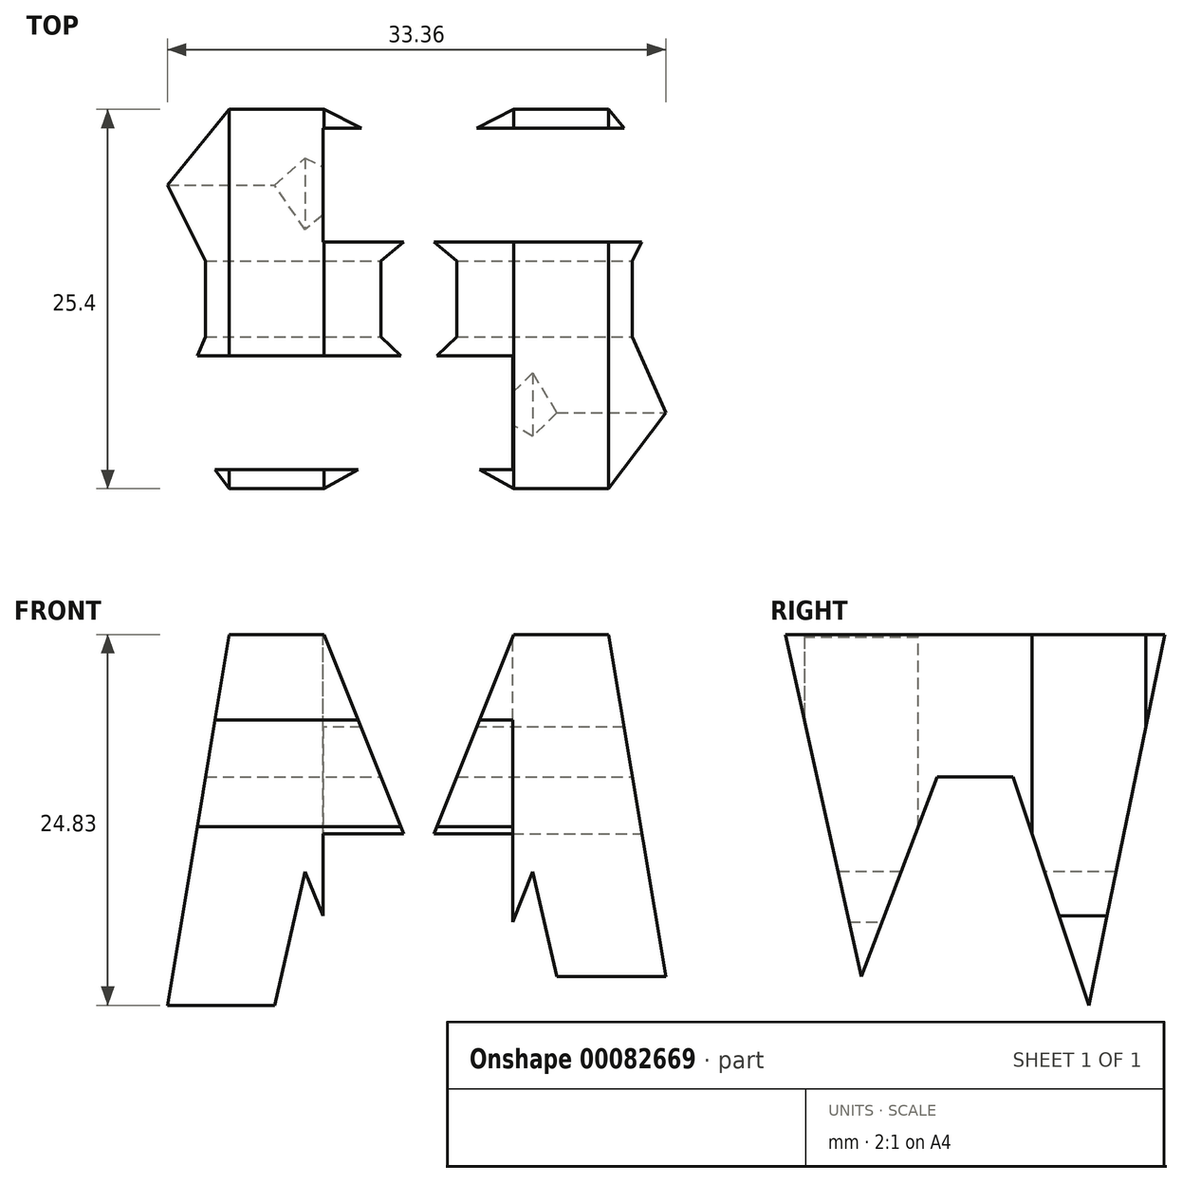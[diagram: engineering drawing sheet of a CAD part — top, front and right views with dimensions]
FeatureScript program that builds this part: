
annotation { "Feature Type Name" : "Feature", "Feature Type Description" : "" }
export const myFeature = defineFeature(function(context is Context, id is Id, definition is map)
    precondition{}
    {
        {
            var Q0;
            Q0=qCreatedBy(makeId("Front.planeOp"),FACE);
            var sketch = newSketch(context, id + "F0", { "sketchPlane" : qUnion([Q0])});
            skLineSegment(sketch, "E0.bottom", {"start": v(19.05, 19.05) * mm, "end": v(-19.05, 19.05) * mm});
            skLineSegment(sketch, "E0.top", {"start": v(19.05, -19.05) * mm, "end": v(-19.05, -19.05) * mm});
            skLineSegment(sketch, "E0.left", {"start": v(19.05, 19.05) * mm, "end": v(19.05, -19.05) * mm});
            skLineSegment(sketch, "E0.right", {"start": v(-19.05, 19.05) * mm, "end": v(-19.05, -19.05) * mm});
            skPoint(sketch, "E0.middle", {"position": v(0, 0) * mm});
            skSolve(sketch);
        }
        {
            var Q0;
            Q0 = qSketchRegion(id + "F0", true);
            extrude(context, id + "F1", {"entities" : qUnion([Q0]), "depth" : 38.1 * mm});
        }
        {
            var Q0;
            Q0=qCreatedBy(makeId("Front.planeOp"),FACE);
            cPlane(context, id + "F2", {"entities" : qUnion([Q0]), "cplaneType" : CPlaneType.OFFSET, "offset" : 38.1 * mm, "width" : 152.4 * mm, "height" : 152.4 * mm});
        }
        {
            var Q0;
            Q0=qCreatedBy(makeId("Top.planeOp"),FACE);
            cPlane(context, id + "F3", {"entities" : qUnion([Q0]), "cplaneType" : CPlaneType.OFFSET, "offset" : 38.1 * mm, "width" : 152.4 * mm, "height" : 152.4 * mm});
        }
        {
            var Q0;
            Q0=qCreatedBy(makeId("Right.planeOp"),FACE);
            cPlane(context, id + "F4", {"entities" : qUnion([Q0]), "cplaneType" : CPlaneType.OFFSET, "offset" : 38.1 * mm, "width" : 152.4 * mm, "height" : 152.4 * mm});
        }
        {
            var Q0;
            Q0=qCreatedBy(id+"F4.planeOp",FACE);
            var sketch = newSketch(context, id + "F5", { "sketchPlane" : qUnion([Q0])});
            skLineSegment(sketch, "E1", {"start": v(0, -19.05) * mm, "end": v(-38.1, -19.05) * mm});
            skLineSegment(sketch, "E2", {"start": v(-38.1, -19.05) * mm, "end": v(-38.1, 19.05) * mm});
            skLineSegment(sketch, "E3", {"start": v(-38.1, 19.05) * mm, "end": v(0, 19.05) * mm});
            skLineSegment(sketch, "E4", {"start": v(0, 19.05) * mm, "end": v(0, -19.05) * mm});
            skLineSegment(sketch, "E5", {"start": v(-38.1, 19.05) * mm, "end": v(-31.75, -19.05) * mm});
            skLineSegment(sketch, "E6", {"start": v(-31.75, -19.05) * mm, "end": v(-25.4, -19.05) * mm});
            skLineSegment(sketch, "E7", {"start": v(-25.4, -19.05) * mm, "end": v(-19.05, -3.17) * mm});
            skLineSegment(sketch, "E8", {"start": v(-19.05, -3.17) * mm, "end": v(-12.7, -19.05) * mm});
            skLineSegment(sketch, "E9", {"start": v(-12.7, -19.05) * mm, "end": v(-6.35, -19.05) * mm});
            skLineSegment(sketch, "E10", {"start": v(-6.35, -19.05) * mm, "end": v(0, 19.05) * mm});
            skLineSegment(sketch, "E11", {"start": v(0, 19.05) * mm, "end": v(-6.35, 19.05) * mm});
            skLineSegment(sketch, "E12", {"start": v(-6.35, 19.05) * mm, "end": v(-11.43, -5.78) * mm});
            skLineSegment(sketch, "E13", {"start": v(-11.43, -5.78) * mm, "end": v(-16.51, 9.53) * mm});
            skLineSegment(sketch, "E14", {"start": v(-16.5, 9.52) * mm, "end": v(-21.59, 9.52) * mm});
            skLineSegment(sketch, "E15", {"start": v(-21.59, 9.52) * mm, "end": v(-26.67, -3.85) * mm});
            skLineSegment(sketch, "E16", {"start": v(-26.67, -3.85) * mm, "end": v(-31.75, 19.05) * mm});
            skLineSegment(sketch, "E17", {"start": v(-31.75, 19.05) * mm, "end": v(-38.1, 19.05) * mm});
            skSolve(sketch);
        }
        {
            var Q0;
            Q0=qCreatedBy(id+"F2.planeOp",FACE);
            var sketch = newSketch(context, id + "F6", { "sketchPlane" : qUnion([Q0])});
            skLineSegment(sketch, "E18", {"start": v(-19.05, 19.05) * mm, "end": v(19.05, 19.05) * mm});
            skLineSegment(sketch, "E19", {"start": v(19.05, 19.05) * mm, "end": v(19.05, -19.05) * mm});
            skLineSegment(sketch, "E20", {"start": v(19.05, -19.05) * mm, "end": v(-19.05, -19.05) * mm});
            skLineSegment(sketch, "E21", {"start": v(-19.05, -19.05) * mm, "end": v(-19.05, 19.05) * mm});
            skLineSegment(sketch, "E22", {"start": v(-12.7, 19.05) * mm, "end": v(-19.05, -19.05) * mm});
            skLineSegment(sketch, "E23", {"start": v(-12.7, -19.05) * mm, "end": v(-7.62, 3.17) * mm});
            skLineSegment(sketch, "E24", {"start": v(-7.62, 3.17) * mm, "end": v(-2.54, -9.5) * mm});
            skLineSegment(sketch, "E25", {"start": v(-2.54, -9.5) * mm, "end": v(2.54, -9.5) * mm});
            skLineSegment(sketch, "E26", {"start": v(2.54, -9.5) * mm, "end": v(7.62, 3.17) * mm});
            skLineSegment(sketch, "E27", {"start": v(7.62, 3.18) * mm, "end": v(12.7, -19.05) * mm});
            skLineSegment(sketch, "E28", {"start": v(12.7, -19.05) * mm, "end": v(19.05, -19.05) * mm});
            skLineSegment(sketch, "E29", {"start": v(19.05, -19.05) * mm, "end": v(12.7, 19.05) * mm});
            skLineSegment(sketch, "E30", {"start": v(12.7, 19.05) * mm, "end": v(6.35, 19.05) * mm});
            skLineSegment(sketch, "E31", {"start": v(6.35, 19.05) * mm, "end": v(0, 3.17) * mm});
            skLineSegment(sketch, "E32", {"start": v(-6.35, 19.05) * mm, "end": v(-12.7, 19.05) * mm});
            skLineSegment(sketch, "E33", {"start": v(-6.35, 19.05) * mm, "end": v(0, 3.17) * mm});
            skSolve(sketch);
        }
        {
            var Q0;
            Q0=makeQuery(id+"F5.imprint","IMPRINT",FACE,{"disambiguationData":[TD([[makeQuery(id+"F5.imprint","IMPRINT",EDGE,{"derivedFrom":sQuery(id+"F5.wireOp",EDGE,"E3")}),-1.0]])]});
            var Q1;
            {var subQ0=sQuery(id+"F5.wireOp",EDGE,"E4");Q1=makeQuery(id+"F5.imprint","IMPRINT",FACE,{"disambiguationData":[TD([[makeQuery(id+"F5.imprint","IMPRINT",EDGE,{"derivedFrom":subQ0}),-1.0]])]});}
            var Q2;
            {var subQ0=sQuery(id+"F5.wireOp",EDGE,"E7");Q2=makeQuery(id+"F5.imprint","IMPRINT",FACE,{"disambiguationData":[TD([[makeQuery(id+"F5.imprint","IMPRINT",EDGE,{"derivedFrom":subQ0}),-1.0]])]});}
            var Q3;
            {var subQ0=sQuery(id+"F5.wireOp",EDGE,"E2");Q3=makeQuery(id+"F5.imprint","IMPRINT",FACE,{"disambiguationData":[TD([[makeQuery(id+"F5.imprint","IMPRINT",EDGE,{"derivedFrom":subQ0}),-1.0]])]});}
            extrude(context, id + "F7", {"entities" : qUnion([Q0, Q1, Q2, Q3]), "operationType" : NewBodyOperationType.REMOVE, "oppositeDirection" : true, "depth" : 58.42 * mm});
        }
        {
            var Q0;
            {var subQ0=sQuery(id+"F6.wireOp",EDGE,"E31");Q0=makeQuery(id+"F6.imprint","IMPRINT",FACE,{"disambiguationData":[TD([[makeQuery(id+"F6.imprint","IMPRINT",EDGE,{"derivedFrom":subQ0}),-1.0]])]});}
            var Q1;
            {var subQ0=sQuery(id+"F6.wireOp",EDGE,"E19");Q1=makeQuery(id+"F6.imprint","IMPRINT",FACE,{"disambiguationData":[TD([[makeQuery(id+"F6.imprint","IMPRINT",EDGE,{"derivedFrom":subQ0}),-1.0]])]});}
            var Q2;
            {var subQ1=sQuery(id+"F6.wireOp",EDGE,"E23");Q2=makeQuery(id+"F6.imprint","IMPRINT",FACE,{"disambiguationData":[TD([[makeQuery(id+"F6.imprint","IMPRINT",EDGE,{"derivedFrom":subQ1}),-1.0]])]});}
            var Q3;
            {var subQ0=sQuery(id+"F6.wireOp",EDGE,"E21");Q3=makeQuery(id+"F6.imprint","IMPRINT",FACE,{"disambiguationData":[TD([[makeQuery(id+"F6.imprint","IMPRINT",EDGE,{"derivedFrom":subQ0}),-1.0]])]});}
            extrude(context, id + "F8", {"entities" : qUnion([Q0, Q1, Q2, Q3]), "operationType" : NewBodyOperationType.REMOVE, "oppositeDirection" : true, "depth" : 38.1 * mm});
        }
        {
            var Q0;
            Q0=qCreatedBy(id+"F3.planeOp",FACE);
            var sketch = newSketch(context, id + "F9", { "sketchPlane" : qUnion([Q0])});
            skLineSegment(sketch, "E34", {"start": v(-19.14, 0) * mm, "end": v(-19.14, -38.1) * mm});
            skLineSegment(sketch, "E35", {"start": v(-19.14, -38.1) * mm, "end": v(18.96, -38.1) * mm});
            skLineSegment(sketch, "E36", {"start": v(18.96, -38.1) * mm, "end": v(18.96, 0) * mm});
            skLineSegment(sketch, "E37", {"start": v(-19.14, 0) * mm, "end": v(18.96, 0) * mm});
            skLineSegment(sketch, "E38", {"start": v(18.96, -7.62) * mm, "end": v(-6.44, -7.62) * mm});
            skLineSegment(sketch, "E39", {"start": v(-6.44, -7.62) * mm, "end": v(-6.44, -15.24) * mm});
            skLineSegment(sketch, "E40", {"start": v(-6.44, -15.24) * mm, "end": v(18.96, -15.24) * mm});
            skLineSegment(sketch, "E41", {"start": v(-19.14, -22.86) * mm, "end": v(6.26, -22.86) * mm});
            skLineSegment(sketch, "E42", {"start": v(6.26, -22.86) * mm, "end": v(6.26, -30.48) * mm});
            skLineSegment(sketch, "E43", {"start": v(6.26, -30.48) * mm, "end": v(-19.14, -30.48) * mm});
            skSolve(sketch);
        }
        {
            var Q0;
            {var subQ0=sQuery(id+"F9.wireOp",EDGE,"E38");Q0=makeQuery(id+"F9.imprint","IMPRINT",FACE,{"disambiguationData":[TD([[makeQuery(id+"F9.imprint","IMPRINT",EDGE,{"derivedFrom":subQ0}),1.0]])]});}
            var Q1;
            {var subQ0=sQuery(id+"F9.wireOp",EDGE,"E41");Q1=makeQuery(id+"F9.imprint","IMPRINT",FACE,{"disambiguationData":[TD([[makeQuery(id+"F9.imprint","IMPRINT",EDGE,{"derivedFrom":subQ0}),-1.0]])]});}
            extrude(context, id + "F10", {"entities" : qUnion([Q0, Q1]), "operationType" : NewBodyOperationType.REMOVE, "oppositeDirection" : true, "depth" : 63.5 * mm});
        }
    });
